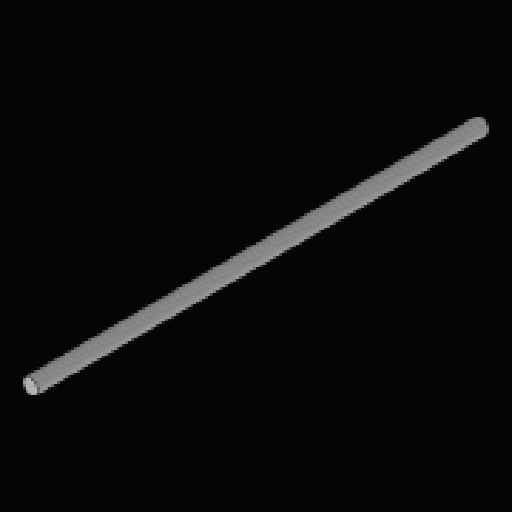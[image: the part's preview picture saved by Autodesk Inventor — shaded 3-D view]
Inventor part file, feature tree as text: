
AUTODESK INVENTOR PART (.ipt)
format: ipt  version: 2023.2 (Build 272271030, 271C)  size: 86,528 bytes
history: native  units: mm
features: extrude x1, thread x1, sketch x1
ambient origin geometry x8: Origin, YZ Plane, XZ Plane, XY Plane, X Axis, Y Axis, Z Axis, Center Point
bodies: Solid1 (feature_tree)
feature tree (3):
  extrude  "Extrusion1"  Depth=87.0mm TaperAngle=0.0deg
  thread  "Thread1"  [1 undecoded]
  sketch  "Sketch1"  dims[d0=3.0mm d1=87.0mm d2=0.0mm d3=90.0mm d4=0.0mm]
note: 1 required parameter value undecoded (feature->parameter linkage not recoverable at this tier; creation-order binding heuristic only, values carry confidence <= 0.55)
